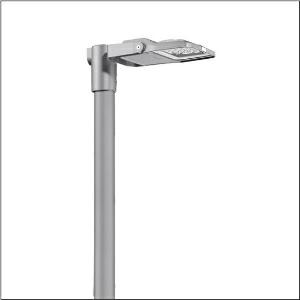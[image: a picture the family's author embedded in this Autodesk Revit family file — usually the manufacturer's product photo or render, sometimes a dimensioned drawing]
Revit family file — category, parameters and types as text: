
# Revit family: floodlight_fl_21_iq_micro___pl43_5xa7762a2a3a_62d6
name_source: partatom
category: Lighting Fixtures
units: mm (PartAtom-declared; Revit-internal decimal feet)

## family parameters
Cut with Voids When Loaded = No
Host = Face
Light Source = No
Part Type = Normal
Room Calculation Point = No
Round Connector Dimension = Use Diameter
Shared = No

## types (1)
- --- (1 x LED, 3040 lm, 23.1 W, 3000K)
    Apparent Load = 23 VA
    CIE Flux Codes = 29 80 99 100 100
    Color Rendering = 70
    Color Temperature = 3000K
    Default Elevation = 1800 mm
    Description = Floodlight FL 21 iQ micro, floodlight, primary light control with lens, of PMMA, primary optical cover: protective disc, of toughened safety glass, transparent, light distribution: PL43, light emission: direct distribution, installation type: surface-mounted, LED, High Power LED, rated luminous flux: 3.040lm, luminous efficacy: 132lm/W, light colour: 730, colour temperature: 3000K, control: Auto-Match, Temp-Guard, Night-Set, Smart-Wire, Desk-Remote (wireless, voltage-free reading and setting of iQ features in the workshop via application-optimized NFC function/RFID function), optimised constant luminous flux control (CLO 2.0), Street-Remote, with terminal, 6-pole, mains connection: 220..240V, AC, 50/60Hz, start of lifetime: 23W, end of service life: 24W, reduction: 11W, luminaire housing, of diecast aluminium, powder-coated, Siteco® metallic grey (DB 702S), corrosivity category C5 mid according to DIN EN ISO 12944, sealing non-destructively replaceable, please order mast flange separately, mast bracket, of steel, galvanised, powder-coated, Siteco® metallic grey (DB 702S), protection rating (complete): IP66, insulation class (complete): insulation class II (safety insulation), certification: CE, ENEC, VDE, protection symbol: D, impact resistance: IK07, permissible operating ambient temperature: -40..+40°C, permissible operating ambient temperature for outdoor applications: -40..+50°C, standard: DIN EN 12944, LABS conformity tested according to VDMA 24364:2018-05, packaging unit: 1 piece

Light Distribution: PL43
    Height = 65 mm
    Lamp = 1 x LED
    Lamp Light Flux = 3040 lm
    Lamp Power = 23.1 W
    Lamp count = 1
    Length = 312 mm
    Luminous efficacy = 132 lm/W
    Manufacturer = Siteco
    ModVariant = No
    Model = 5XA7762A2A3A
    Number of Poles = 1
    OnlyDefault = Yes
    Power Factor = 1
    Product Name = Floodlight FL 21 iQ micro | PL43
    Product group = floodlight | pylon annexe
    ProductGroupID = 6200
    Protection Class = Protection class II
    Protection Degree = IP 66
    RLX_Detail_Level = 1
    RLX_Emergency_Light_Flux = 0 lm
    RLX_Emergency_Type = 0
    RLX_Emergency_Type_DB = No
    RlxData = <blob elided: 101925 chars, md5=0cdf2fef>
    Socket = socket
    Standby Power = 0 W
    System Light Flux = 3040 lm
    System Power = 23 W
    Type Comments = factory setting: luminous flux: 100 % | dim-lin: 254 | 455 mA
    Type Image = l_1007121.jpg
    URL = http://relux.com
    VarID = @adj_147839
    Voltage = 0 V
    Weight = 0.00 kg
    Width = 230 mm

## geometry (parser evidence)
native form markers: Blend x4, Sweep x11
no freeform markers — native parametric forms only
